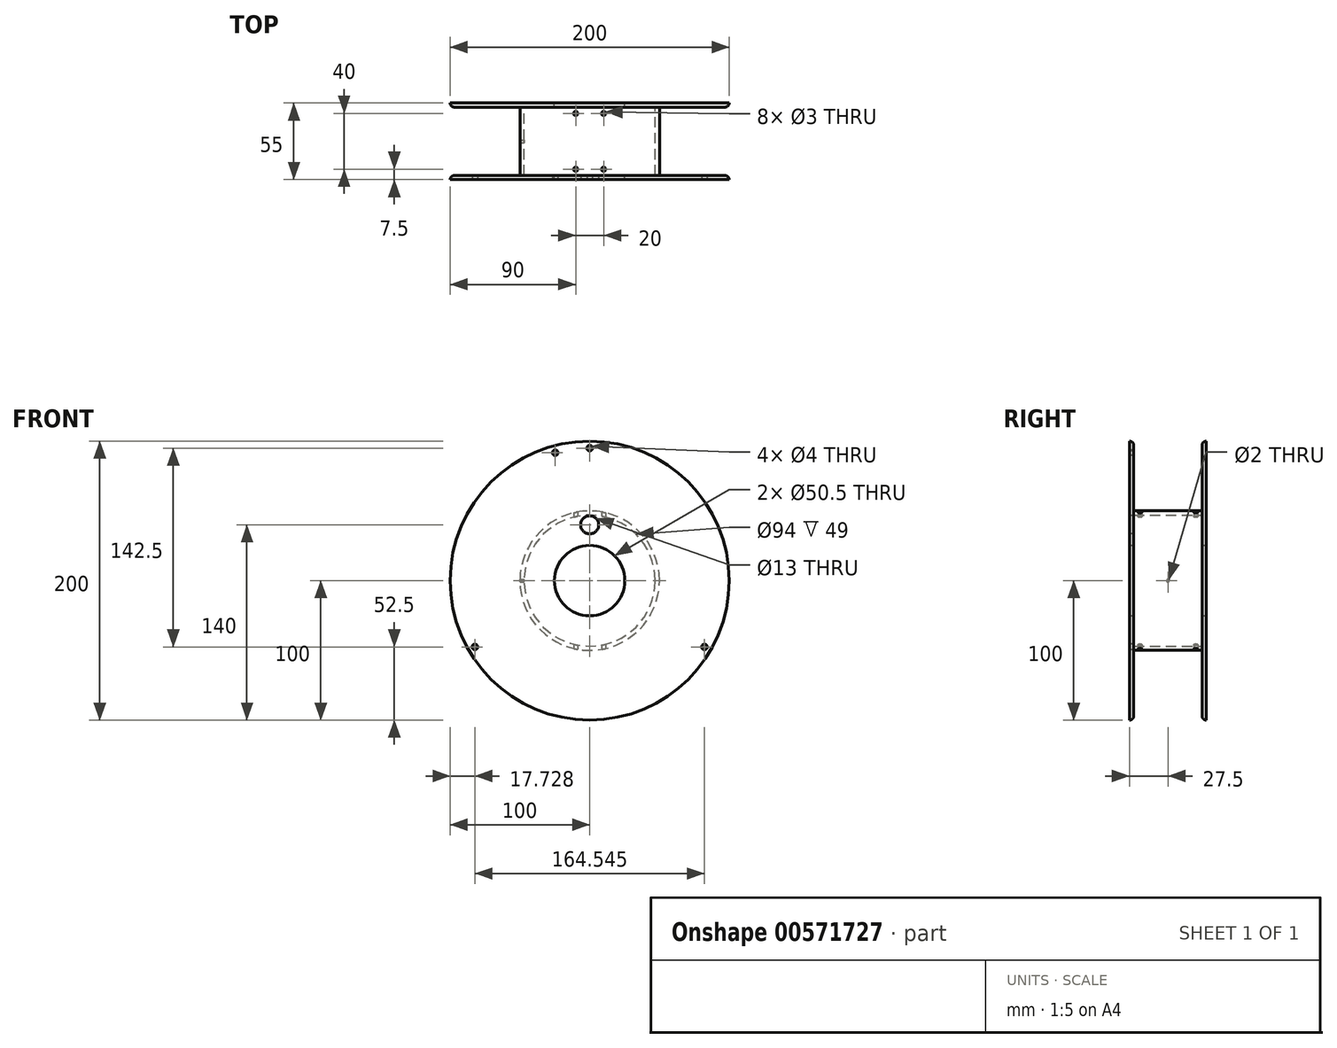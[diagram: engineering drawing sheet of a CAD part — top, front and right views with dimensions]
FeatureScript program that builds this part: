
annotation { "Feature Type Name" : "Feature", "Feature Type Description" : "" }
export const myFeature = defineFeature(function(context is Context, id is Id, definition is map)
    precondition{}
    {
        {
            var Q0;
            Q0=qCreatedBy(makeId("Right.planeOp"),FACE);
            var sketch = newSketch(context, id + "F0", { "sketchPlane" : qUnion([Q0])});
            skLineSegment(sketch, "E0", {"start": v(-27.5, 100) * mm, "end": v(-27.5, 25.25) * mm});
            skLineSegment(sketch, "E1", {"start": v(-27.5, 25.25) * mm, "end": v(-24.5, 25.25) * mm});
            skLineSegment(sketch, "E2", {"start": v(-24.5, 25.25) * mm, "end": v(-24.5, 47) * mm});
            skLineSegment(sketch, "E3", {"start": v(-24.5, 47) * mm, "end": v(24.5, 47) * mm});
            skLineSegment(sketch, "E4", {"start": v(-27.5, 100) * mm, "end": v(-24.5, 100) * mm});
            skLineSegment(sketch, "E5", {"start": v(-24.5, 100) * mm, "end": v(-24.5, 50) * mm});
            skLineSegment(sketch, "E6", {"start": v(-24.5, 50) * mm, "end": v(24.5, 50) * mm});
            skLineSegment(sketch, "E7", {"start": v(0, 0) * mm, "end": v(0, 43.55) * mm, "construction": true});
            skLineSegment(sketch, "E8.MirrorCS", {"start": v(24.5, 100) * mm, "end": v(24.5, 50) * mm});
            skLineSegment(sketch, "E9.MirrorCS", {"start": v(27.5, 100) * mm, "end": v(24.5, 100) * mm});
            skLineSegment(sketch, "E10.MirrorCS", {"start": v(27.5, 100) * mm, "end": v(27.5, 25.25) * mm});
            skLineSegment(sketch, "E11.MirrorCS", {"start": v(24.5, 25.25) * mm, "end": v(24.5, 47) * mm});
            skLineSegment(sketch, "E12.MirrorCS", {"start": v(27.5, 25.25) * mm, "end": v(24.5, 25.25) * mm});
            skLineSegment(sketch, "E13", {"start": v(0, 0) * mm, "end": v(-201.5, 0) * mm, "construction": true});
            skLineSegment(sketch, "E14", {"start": v(24.5, 50) * mm, "end": v(24.5, 47) * mm});
            skLineSegment(sketch, "E15", {"start": v(-24.5, 50) * mm, "end": v(-24.5, 47) * mm});
            skSolve(sketch);
        }
        {
            var Q0;
            Q0=makeQuery(id+"F0.imprint","IMPRINT",FACE,{"disambiguationData":[TD([[makeQuery(id+"F0.imprint","IMPRINT",EDGE,{"derivedFrom":sQuery(id+"F0.wireOp",EDGE,"E0")}),1.0]])]});
            var Q1;
            Q1=makeQuery(id+"F0.imprint","IMPRINT",FACE,{"disambiguationData":[TD([[makeQuery(id+"F0.imprint","IMPRINT",EDGE,{"derivedFrom":sQuery(id+"F0.wireOp",EDGE,"E8.MirrorCS")}),1.0]])]});
            var Q2;
            Q2=sQuery(id+"F0.wireOp",EDGE,"E13");
            revolve(context, id + "F1", {"entities" : qUnion([Q0, Q1]), "axis" : qUnion([Q2]), "revolveType" : RevolveType.FULL});
        }
        {
            var Q0;
            Q0=makeQuery(id+"F0.imprint","IMPRINT",FACE,{"disambiguationData":[TD([[makeQuery(id+"F0.imprint","IMPRINT",EDGE,{"derivedFrom":sQuery(id+"F0.wireOp",EDGE,"E3")}),1.0]])]});
            var Q1;
            Q1=sQuery(id+"F0.wireOp",EDGE,"E13");
            revolve(context, id + "F2", {"entities" : qUnion([Q0]), "axis" : qUnion([Q1]), "revolveType" : RevolveType.FULL});
        }
        {
            var Q0;
            Q0=makeQuery(id+"F1.opRevolve","SWEPT_EDGE",EDGE,{"disambiguationData":[OSD([sQuery(id+"F0.wireOp",EDGE,"E6"),sQuery(id+"F0.wireOp",EDGE,"E8.MirrorCS")])]});
            var Q1;
            Q1=makeQuery(id+"F1.opRevolve","SWEPT_EDGE",EDGE,{"disambiguationData":[OSD([sQuery(id+"F0.wireOp",EDGE,"E5"),sQuery(id+"F0.wireOp",EDGE,"E6")])]});
            fillet(context, id + "F3", {"entities" : qUnion([Q0, Q1]), "radius" : 3 * mm, "tangentPropagation" : true, "allowEdgeOverflow" : false});
        }
        {
            var Q0;
            Q0=makeQuery(id+"F1.opRevolve","SWEPT_FACE",FACE,{"disambiguationData":[OSD([sQuery(id+"F0.wireOp",EDGE,"E0")])]});
            var sketch = newSketch(context, id + "F4", { "sketchPlane" : qUnion([Q0])});
            skCircle(sketch, "E16", {"center": v(0, 95) * mm, "radius": 2 * mm});
            skCircle(sketch, "E17", {"center": v(0, 40) * mm, "radius": 6.5 * mm});
            skLineSegment(sketch, "E18", {"start": v(0, 0) * mm, "end": v(0, 95) * mm, "construction": true});
            skCircle(sketch, "E19.1.0", {"center": v(-82.27, -47.5) * mm, "radius": 2 * mm});
            skCircle(sketch, "E19.2.0", {"center": v(82.27, -47.5) * mm, "radius": 2 * mm});
            skPoint(sketch, "E19.center", {"position": v(0, 0) * mm});
            skArc(sketch, "E20", {"start": v(0, 95) * mm, "mid": v(-12.46, 94.18) * mm, "end": v(-24.71, 91.73) * mm, "construction": true});
            skCircle(sketch, "E21", {"center": v(-24.71, 91.73) * mm, "radius": 2 * mm});
            skSolve(sketch);
        }
        {
            var Q0;
            Q0=makeQuery(id+"F4.imprint","IMPRINT",FACE,{"disambiguationData":[TD([[makeQuery(id+"F4.imprint","IMPRINT",EDGE,{"derivedFrom":sQuery(id+"F4.wireOp",EDGE,"E16")}),1.0]])]});
            var Q1;
            Q1=makeQuery(id+"F4.imprint","IMPRINT",FACE,{"disambiguationData":[TD([[makeQuery(id+"F4.imprint","IMPRINT",EDGE,{"derivedFrom":sQuery(id+"F4.wireOp",EDGE,"E17")}),1.0]])]});
            var Q2;
            Q2=makeQuery(id+"F4.imprint","IMPRINT",FACE,{"disambiguationData":[TD([[makeQuery(id+"F4.imprint","IMPRINT",EDGE,{"derivedFrom":sQuery(id+"F4.wireOp",EDGE,"E21")}),1.0]])]});
            var Q3;
            Q3=makeQuery(id+"F4.imprint","IMPRINT",FACE,{"disambiguationData":[TD([[makeQuery(id+"F4.imprint","IMPRINT",EDGE,{"derivedFrom":sQuery(id+"F4.wireOp",EDGE,"E19.1.0")}),1.0]])]});
            var Q4;
            Q4=makeQuery(id+"F4.imprint","IMPRINT",FACE,{"disambiguationData":[TD([[makeQuery(id+"F4.imprint","IMPRINT",EDGE,{"derivedFrom":sQuery(id+"F4.wireOp",EDGE,"E19.2.0")}),1.0]])]});
            extrude(context, id + "F5", {"entities" : qUnion([Q0, Q1, Q2, Q3, Q4]), "operationType" : NewBodyOperationType.REMOVE, "oppositeDirection" : true, "depth" : 10 * mm, "offsetDistance" : 25 * mm});
        }
        {
            var Q0;
            Q0=qCreatedBy(makeId("Top.planeOp"),FACE);
            var sketch = newSketch(context, id + "F6", { "sketchPlane" : qUnion([Q0])});
            skCircle(sketch, "E22", {"center": v(10, -20) * mm, "radius": 1.5 * mm});
            skLineSegment(sketch, "E23", {"start": v(0, 45.27) * mm, "end": v(0, -37.66) * mm, "construction": true});
            skCircle(sketch, "E24.MirrorC", {"center": v(-10, -20) * mm, "radius": 1.5 * mm});
            skLineSegment(sketch, "E25", {"start": v(-32.93, 0) * mm, "end": v(60.57, 0) * mm, "construction": true});
            skCircle(sketch, "E26.MirrorC", {"center": v(-10, 20) * mm, "radius": 1.5 * mm});
            skCircle(sketch, "E27.MirrorC", {"center": v(10, 20) * mm, "radius": 1.5 * mm});
            skSolve(sketch);
        }
        {
            var Q0;
            Q0 = qSketchRegion(id + "F6", true);
            extrude(context, id + "F7", {"entities" : qUnion([Q0]), "operationType" : NewBodyOperationType.REMOVE, "endBound" : BoundingType.THROUGH_ALL, "depth" : 25 * mm, "offsetDistance" : 25 * mm, "hasSecondDirection" : true, "secondDirectionBound" : SecondDirectionBoundingType.THROUGH_ALL, "secondDirectionOppositeDirection" : true, "secondDirectionDepth" : 25 * mm});
        }
        {
            var Q0;
            Q0=qCreatedBy(makeId("Right.planeOp"),FACE);
            var sketch = newSketch(context, id + "F8", { "sketchPlane" : qUnion([Q0])});
            skCircle(sketch, "E28", {"center": v(0, 0) * mm, "radius": 1 * mm});
            skSolve(sketch);
        }
        {
            var Q0;
            Q0=makeQuery(id+"F8.imprint","IMPRINT",FACE,{"disambiguationData":[TD([[makeQuery(id+"F8.imprint","IMPRINT",EDGE,{"derivedFrom":sQuery(id+"F8.wireOp",EDGE,"E28")}),1.0]])]});
            extrude(context, id + "F9", {"entities" : qUnion([Q0]), "operationType" : NewBodyOperationType.REMOVE, "endBound" : BoundingType.THROUGH_ALL, "oppositeDirection" : true, "depth" : 25 * mm, "offsetDistance" : 25 * mm});
        }
    });
